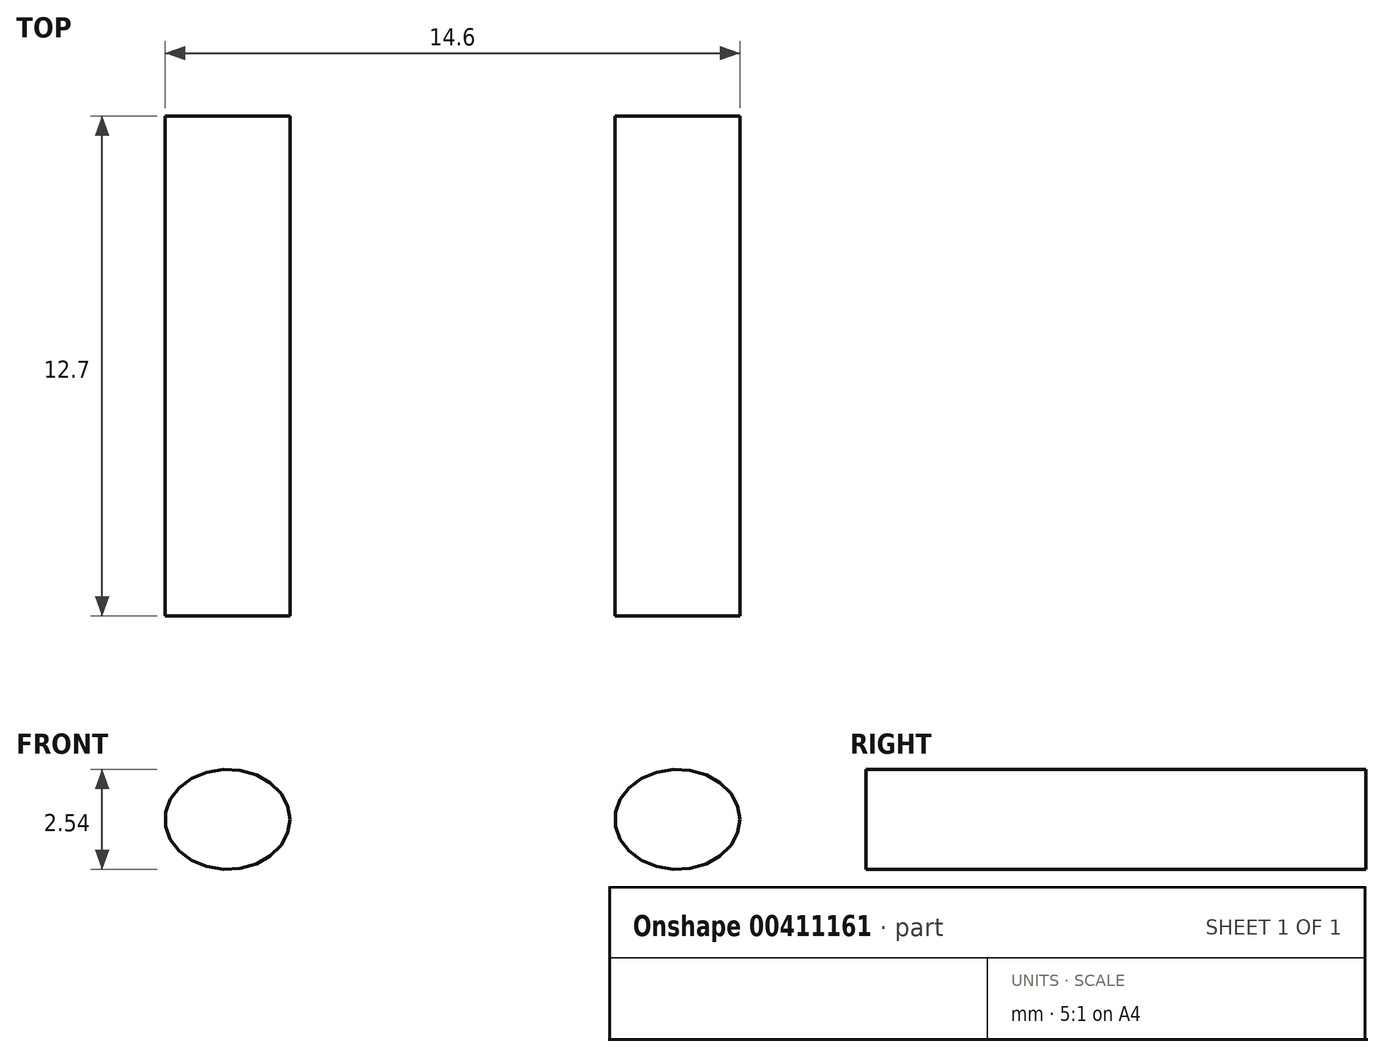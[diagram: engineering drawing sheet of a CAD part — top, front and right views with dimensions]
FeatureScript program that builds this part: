
annotation { "Feature Type Name" : "Feature", "Feature Type Description" : "" }
export const myFeature = defineFeature(function(context is Context, id is Id, definition is map)
    precondition{}
    {
        {
            var Q0;
            Q0=qCreatedBy(makeId("Front.planeOp"),FACE);
            var sketch = newSketch(context, id + "F0", { "sketchPlane" : qUnion([Q0])});
            skEllipse(sketch, "E0", {"center": v(5.72, 0) * mm, "majorRadius": 1.59 * mm, "minorRadius": 1.27 * mm, "majorAxis": v(1, 0)});
            skEllipse(sketch, "E1", {"center": v(-5.72, 0) * mm, "majorRadius": 1.59 * mm, "minorRadius": 1.27 * mm, "majorAxis": v(1, 0)});
            skSolve(sketch);
        }
        {
            var Q0;
            Q0=makeQuery(id+"F0.imprint","IMPRINT",FACE,{"disambiguationData":[TD([[makeQuery(id+"F0.imprint","IMPRINT",EDGE,{"derivedFrom":sQuery(id+"F0.wireOp",EDGE,"E1")}),1.0]])]});
            var Q1;
            Q1=makeQuery(id+"F0.imprint","IMPRINT",FACE,{"disambiguationData":[TD([[makeQuery(id+"F0.imprint","IMPRINT",EDGE,{"derivedFrom":sQuery(id+"F0.wireOp",EDGE,"E0")}),1.0]])]});
            extrude(context, id + "F1", {"entities" : qUnion([Q0, Q1]), "endBound" : BoundingType.SYMMETRIC, "depth" : 12.7 * mm});
        }
    });
